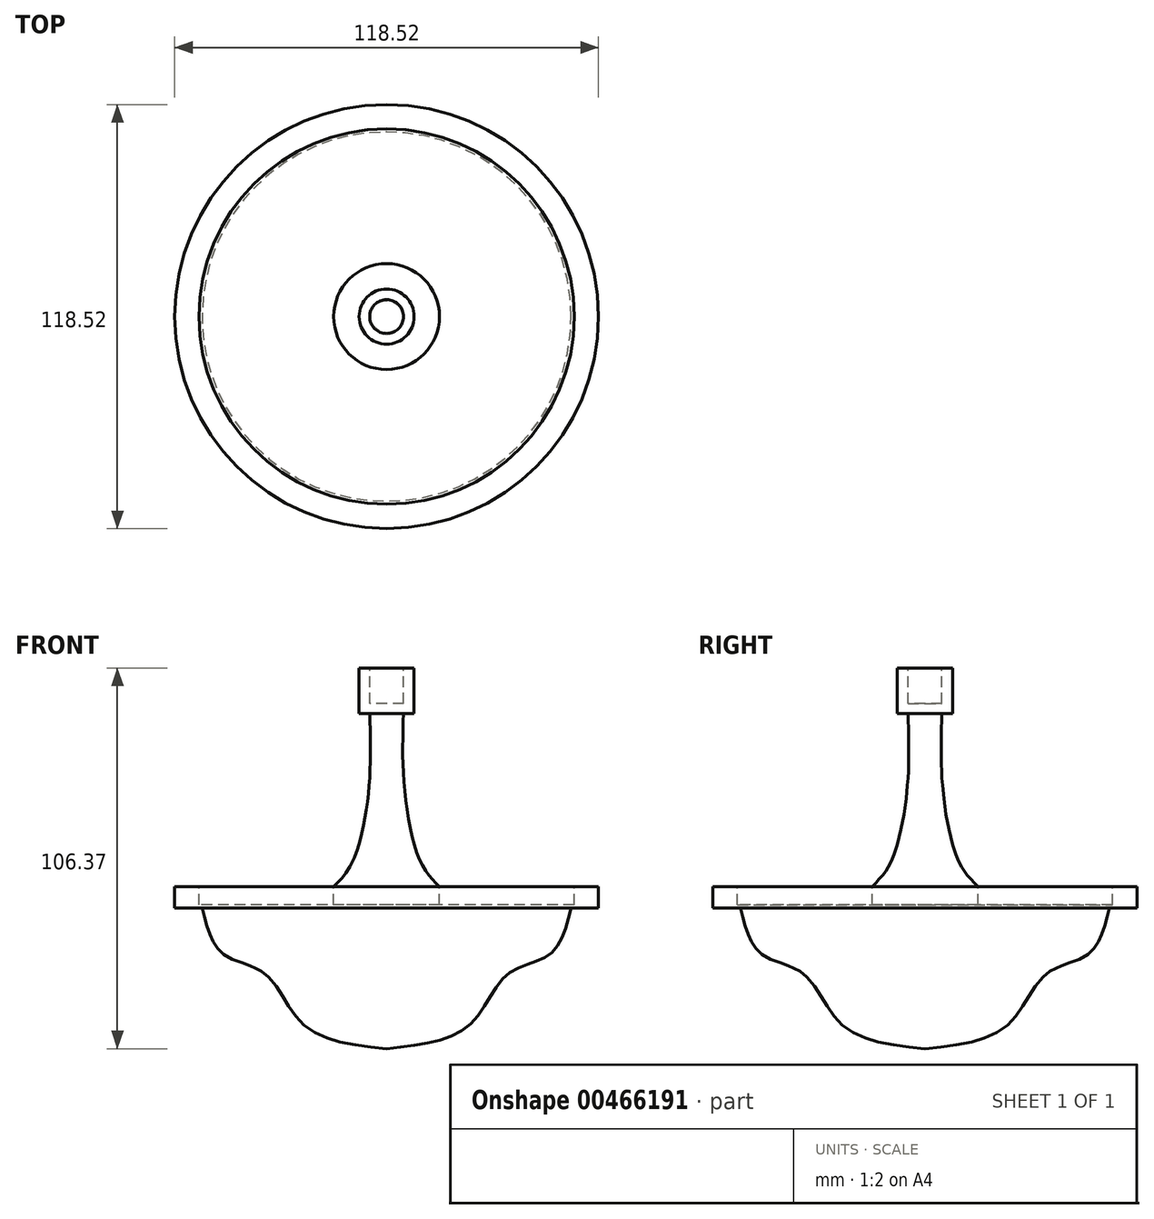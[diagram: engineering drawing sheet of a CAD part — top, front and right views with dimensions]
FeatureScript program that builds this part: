
annotation { "Feature Type Name" : "Feature", "Feature Type Description" : "" }
export const myFeature = defineFeature(function(context is Context, id is Id, definition is map)
    precondition{}
    {
        {
            var Q0;
            Q0=qCreatedBy(makeId("Front.planeOp"),FACE);
            var sketch = newSketch(context, id + "F0", { "sketchPlane" : qUnion([Q0])});
            skLineSegment(sketch, "E0", {"start": v(56.37, -9.6) * mm, "end": v(51.6, -9.6) * mm});
            skFitSpline(sketch, "E1", {"points": [v(51.6, -9.6) * mm, v(45.81, -22.32) * mm, v(33.87, -28.1) * mm, v(23.08, -42.36) * mm, v(0, -48.92) * mm], "startDerivative": vector(-16.47, -66.73) * mm, "endDerivative": vector(-89.58, -9.42) * mm});
            skLineSegment(sketch, "E2", {"start": v(56.37, -9.6) * mm, "end": v(59.26, -9.6) * mm});
            skLineSegment(sketch, "E3", {"start": v(59.26, -9.6) * mm, "end": v(59.26, -3.6) * mm});
            skLineSegment(sketch, "E4", {"start": v(59.26, -3.6) * mm, "end": v(14.8, -3.6) * mm});
            skFitSpline(sketch, "E5", {"points": [v(14.8, -3.6) * mm, v(9.53, 3.28) * mm, v(4.95, 24.13) * mm, v(4.72, 44.75) * mm], "startDerivative": vector(-23.11, 22.74) * mm, "endDerivative": vector(1.66, 52.9) * mm});
            skLineSegment(sketch, "E6", {"start": v(4.72, 44.75) * mm, "end": v(7.7, 44.75) * mm});
            skLineSegment(sketch, "E7", {"start": v(7.7, 44.75) * mm, "end": v(7.7, 57.45) * mm});
            skLineSegment(sketch, "E8", {"start": v(7.7, 57.45) * mm, "end": v(0, 57.45) * mm});
            skLineSegment(sketch, "E9", {"start": v(0, 57.45) * mm, "end": v(0, -48.92) * mm});
            skSolve(sketch);
        }
        {
            var Q0;
            Q0=makeQuery(id+"F0.imprint","IMPRINT",FACE,{"disambiguationData":[TD([[makeQuery(id+"F0.imprint","IMPRINT",EDGE,{"derivedFrom":sQuery(id+"F0.wireOp",EDGE,"E0")}),-1.0]])]});
            var Q1;
            Q1=sQuery(id+"F0.wireOp",EDGE,"E9");
            revolve(context, id + "F1", {"entities" : qUnion([Q0]), "axis" : qUnion([Q1]), "revolveType" : RevolveType.FULL});
        }
        {
            var Q0;
            Q0=makeQuery(id+"F1.opRevolve","SWEPT_FACE",FACE,{"disambiguationData":[OSD([sQuery(id+"F0.wireOp",EDGE,"E4")])]});
            var sketch = newSketch(context, id + "F2", { "sketchPlane" : qUnion([Q0])});
            skCircle(sketch, "E10", {"center": v(0, 0) * mm, "radius": 52.46 * mm});
            skSolve(sketch);
        }
        {
            var Q0;
            Q0=makeQuery(id+"F2.imprint","IMPRINT",FACE,{"disambiguationData":[TD([[makeQuery(id+"F2.imprint","IMPRINT",EDGE,{"derivedFrom":sQuery(id+"F2.wireOp",EDGE,"E10")}),1.0]])]});
            var Q1;
            Q1=sQuery(id+"F2.wireOp",EDGE,"E10");
            extrude(context, id + "F3", {"entities" : qUnion([Q0]), "operationType" : NewBodyOperationType.REMOVE, "surfaceEntities" : qUnion([Q1]), "oppositeDirection" : true, "depth" : 5.08 * mm});
        }
        {
            var Q0;
            Q0=makeQuery(id+"F1.opRevolve","SWEPT_FACE",FACE,{"disambiguationData":[OSD([sQuery(id+"F0.wireOp",EDGE,"E8")])]});
            var sketch = newSketch(context, id + "F4", { "sketchPlane" : qUnion([Q0])});
            skCircle(sketch, "E11", {"center": v(0, 0) * mm, "radius": 4.73 * mm});
            skSolve(sketch);
        }
        {
            var Q0;
            Q0=makeQuery(id+"F4.imprint","IMPRINT",FACE,{"disambiguationData":[TD([[makeQuery(id+"F4.imprint","IMPRINT",EDGE,{"derivedFrom":sQuery(id+"F4.wireOp",EDGE,"E11")}),1.0]])]});
            extrude(context, id + "F5", {"entities" : qUnion([Q0]), "operationType" : NewBodyOperationType.REMOVE, "oppositeDirection" : true, "depth" : 9.9 * mm});
        }
    });
